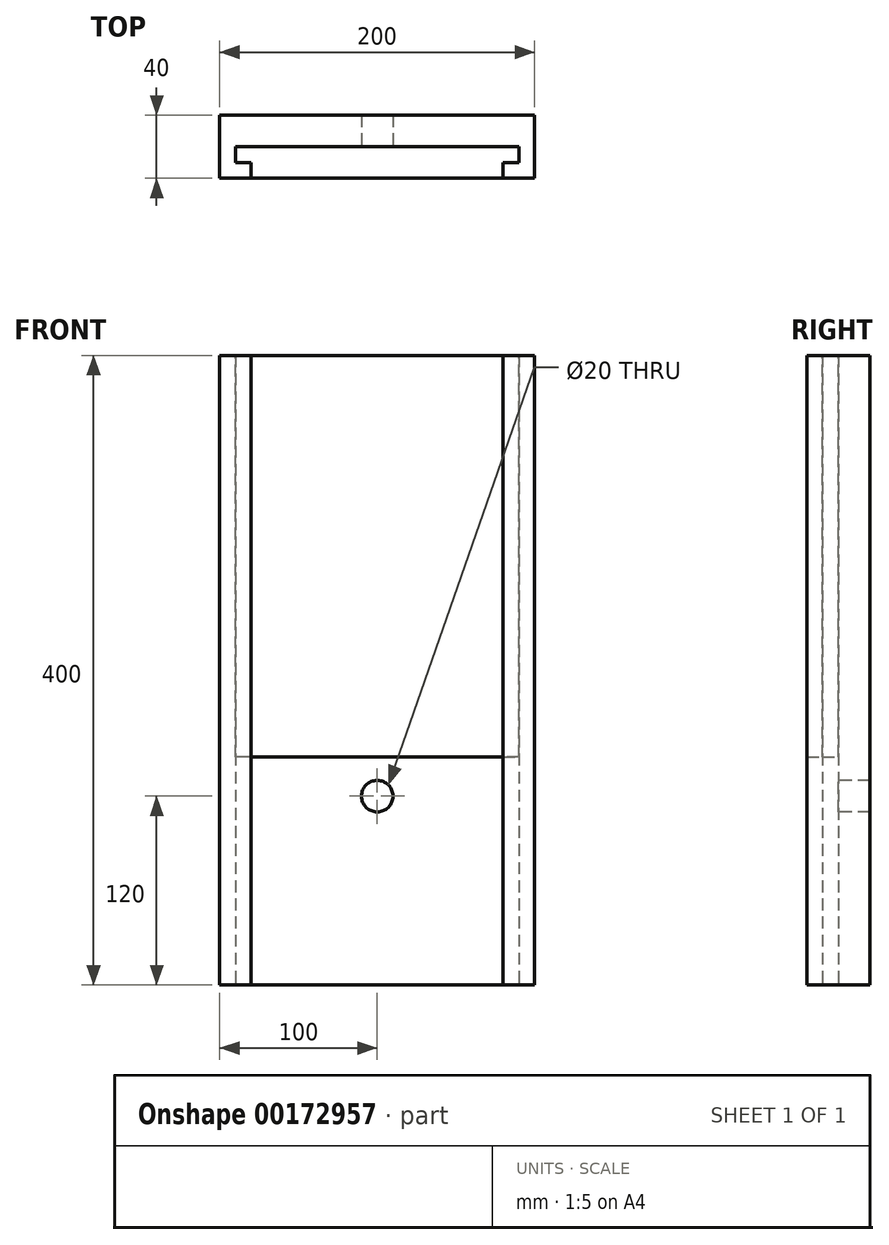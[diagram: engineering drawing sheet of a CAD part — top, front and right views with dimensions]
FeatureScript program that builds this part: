
annotation { "Feature Type Name" : "Feature", "Feature Type Description" : "" }
export const myFeature = defineFeature(function(context is Context, id is Id, definition is map)
    precondition{}
    {
        {
            var Q0;
            Q0=qCreatedBy(makeId("Top.planeOp"),FACE);
            var sketch = newSketch(context, id + "F0", { "sketchPlane" : qUnion([Q0])});
            skLineSegment(sketch, "E0", {"start": v(80, 0) * mm, "end": v(80, 10) * mm});
            skLineSegment(sketch, "E1", {"start": v(80, 10) * mm, "end": v(90, 10) * mm});
            skLineSegment(sketch, "E2", {"start": v(90, 10) * mm, "end": v(90, 20) * mm});
            skLineSegment(sketch, "E3", {"start": v(90, 20) * mm, "end": v(0, 20) * mm});
            skLineSegment(sketch, "E4", {"start": v(0, 20) * mm, "end": v(0, 40) * mm});
            skLineSegment(sketch, "E5", {"start": v(0, 40) * mm, "end": v(100, 40) * mm});
            skLineSegment(sketch, "E6", {"start": v(100, 40) * mm, "end": v(100, 0) * mm});
            skLineSegment(sketch, "E7", {"start": v(100, 0) * mm, "end": v(80, 0) * mm});
            skLineSegment(sketch, "E8", {"start": v(0, 0) * mm, "end": v(0, 40) * mm, "construction": true});
            skLineSegment(sketch, "E9.MirrorCS", {"start": v(0, 40) * mm, "end": v(-100, 40) * mm});
            skLineSegment(sketch, "E10.MirrorCS", {"start": v(-90, 20) * mm, "end": v(0, 20) * mm});
            skLineSegment(sketch, "E11.MirrorCS", {"start": v(-90, 10) * mm, "end": v(-90, 20) * mm});
            skLineSegment(sketch, "E12.MirrorCS", {"start": v(-80, 10) * mm, "end": v(-90, 10) * mm});
            skLineSegment(sketch, "E13.MirrorCS", {"start": v(-80, 0) * mm, "end": v(-80, 10) * mm});
            skLineSegment(sketch, "E14.MirrorCS", {"start": v(-100, 0) * mm, "end": v(-80, 0) * mm});
            skLineSegment(sketch, "E15.MirrorCS", {"start": v(-100, 40) * mm, "end": v(-100, 0) * mm});
            skSolve(sketch);
        }
        {
            var Q0;
            Q0 = qSketchRegion(id + "F0", true);
            extrude(context, id + "F1", {"entities" : qUnion([Q0]), "depth" : 280 * mm, "hasSecondDirection" : true, "secondDirectionOppositeDirection" : true, "secondDirectionDepth" : 120 * mm});
        }
        {
            var Q0;
            Q0=makeQuery(id+"F1.opExtrude","SWEPT_FACE",FACE,{"disambiguationData":[OSD([sQuery(id+"F0.wireOp",EDGE,"E3"),sQuery(id+"F0.wireOp",EDGE,"E10.MirrorCS")])]});
            var sketch = newSketch(context, id + "F2", { "sketchPlane" : qUnion([Q0])});
            skCircle(sketch, "E16", {"center": v(0, 0) * mm, "radius": 10 * mm});
            skSolve(sketch);
        }
        {
            var Q0;
            Q0 = qSketchRegion(id + "F2", true);
            extrude(context, id + "F3", {"entities" : qUnion([Q0]), "operationType" : NewBodyOperationType.REMOVE, "oppositeDirection" : true, "depth" : 20 * mm});
        }
        {
            var Q0;
            Q0=makeQuery(id+"F1.opExtrude","CAP_FACE",FACE,{"disambiguationData":[OSD([sQuery(id+"F0.wireOp",EDGE,"E0"),sQuery(id+"F0.wireOp",EDGE,"E1"),sQuery(id+"F0.wireOp",EDGE,"E2"),sQuery(id+"F0.wireOp",EDGE,"E3"),sQuery(id+"F0.wireOp",EDGE,"E5"),sQuery(id+"F0.wireOp",EDGE,"E6"),sQuery(id+"F0.wireOp",EDGE,"E7"),sQuery(id+"F0.wireOp",EDGE,"E9.MirrorCS"),sQuery(id+"F0.wireOp",EDGE,"E10.MirrorCS"),sQuery(id+"F0.wireOp",EDGE,"E11.MirrorCS"),sQuery(id+"F0.wireOp",EDGE,"E12.MirrorCS"),sQuery(id+"F0.wireOp",EDGE,"E13.MirrorCS"),sQuery(id+"F0.wireOp",EDGE,"E14.MirrorCS"),sQuery(id+"F0.wireOp",EDGE,"E15.MirrorCS")])],"isStart":false});
            var sketch = newSketch(context, id + "F4", { "sketchPlane" : qUnion([Q0])});
            skLineSegment(sketch, "E17", {"start": v(-90, 20) * mm, "end": v(-90, 10) * mm});
            skLineSegment(sketch, "E18", {"start": v(-90, 10) * mm, "end": v(-80, 10) * mm});
            skLineSegment(sketch, "E19", {"start": v(-80, 10) * mm, "end": v(-80, 0) * mm});
            skLineSegment(sketch, "E20", {"start": v(-80, 0) * mm, "end": v(80, 0) * mm});
            skLineSegment(sketch, "E21", {"start": v(80, 0) * mm, "end": v(80, 10) * mm});
            skLineSegment(sketch, "E22", {"start": v(80, 10) * mm, "end": v(90, 10) * mm});
            skLineSegment(sketch, "E23", {"start": v(90, 10) * mm, "end": v(90, 20) * mm});
            skLineSegment(sketch, "E24", {"start": v(90, 20) * mm, "end": v(-90, 20) * mm});
            skSolve(sketch);
        }
        {
            var Q0;
            Q0 = qSketchRegion(id + "F4", true);
            extrude(context, id + "F5", {"entities" : qUnion([Q0]), "oppositeDirection" : true, "depth" : 255 * mm});
        }
    });
